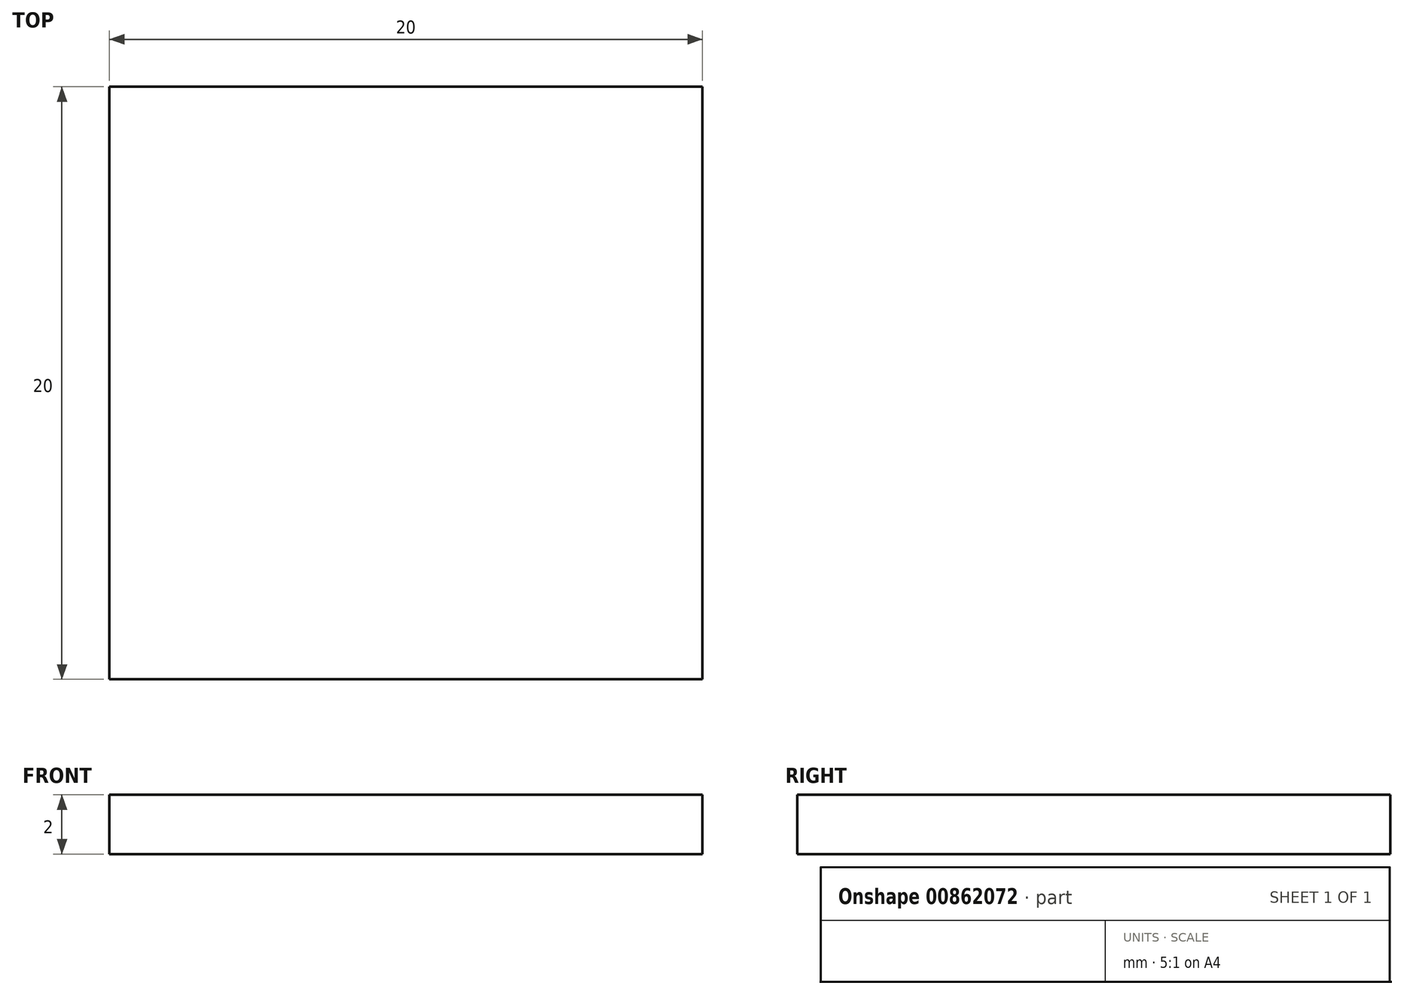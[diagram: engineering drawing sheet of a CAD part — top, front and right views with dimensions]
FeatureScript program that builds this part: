
annotation { "Feature Type Name" : "Feature", "Feature Type Description" : "" }
export const myFeature = defineFeature(function(context is Context, id is Id, definition is map)
    precondition{}
    {
        {
            var Q0;
            Q0=qCreatedBy(makeId("Top.planeOp"),FACE);
            var sketch = newSketch(context, id + "F0", { "sketchPlane" : qUnion([Q0])});
            skLineSegment(sketch, "E0.bottom", {"start": v(-10, 10) * mm, "end": v(10, 10) * mm});
            skLineSegment(sketch, "E0.top", {"start": v(-10, -10) * mm, "end": v(10, -10) * mm});
            skLineSegment(sketch, "E0.left", {"start": v(-10, 10) * mm, "end": v(-10, -10) * mm});
            skLineSegment(sketch, "E0.right", {"start": v(10, 10) * mm, "end": v(10, -10) * mm});
            skPoint(sketch, "E0.middle", {"position": v(0, 0) * mm});
            skSolve(sketch);
        }
        {
            var Q0;
            Q0 = qSketchRegion(id + "F0", true);
            extrude(context, id + "F1", {"entities" : qUnion([Q0]), "depth" : 2 * mm, "offsetDistance" : 25 * mm});
        }
    });
